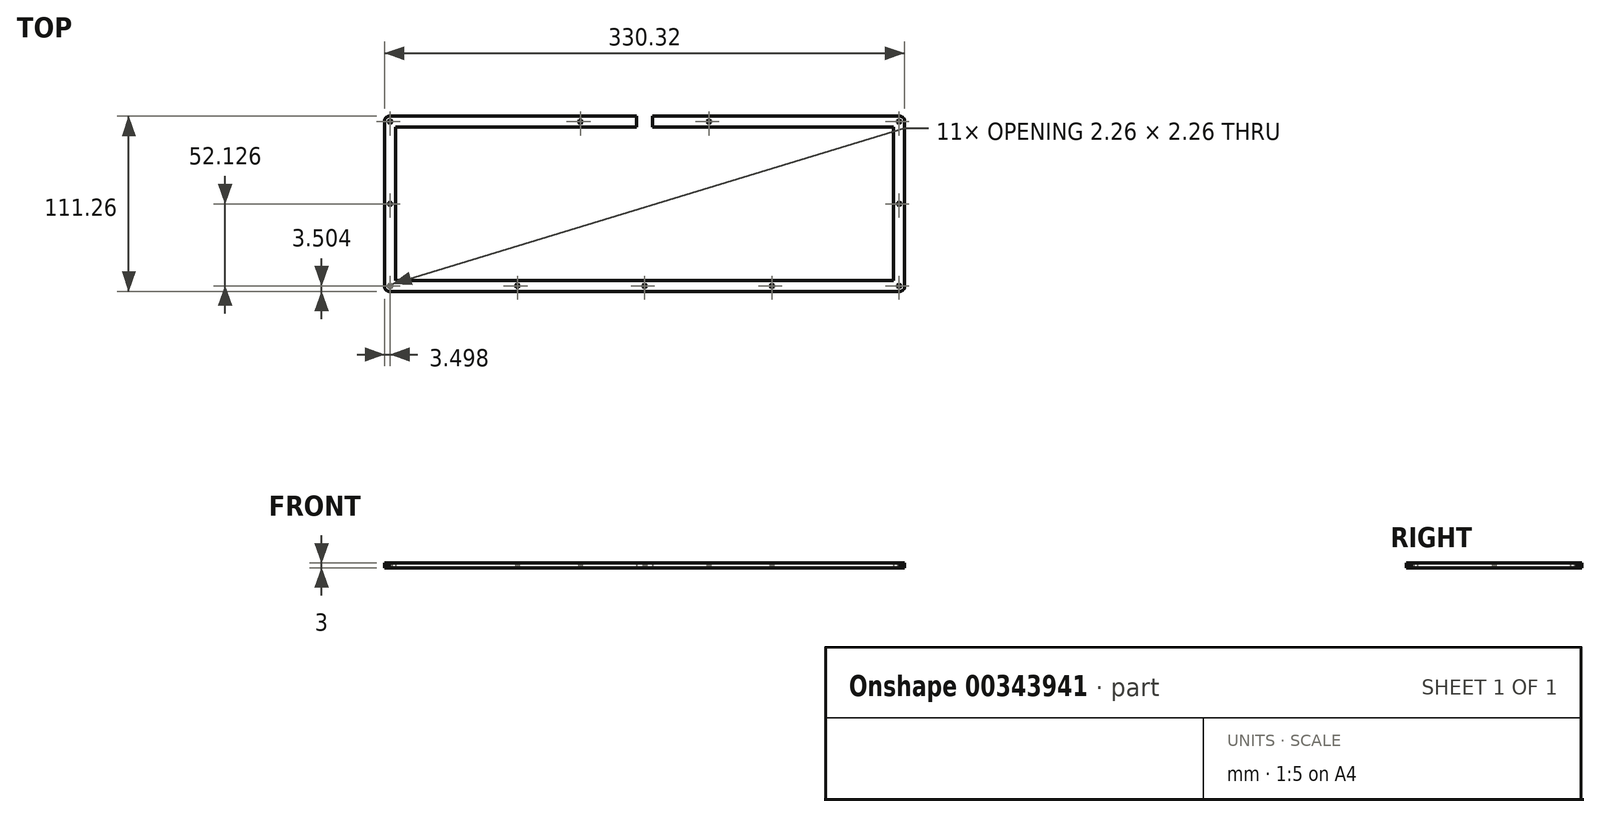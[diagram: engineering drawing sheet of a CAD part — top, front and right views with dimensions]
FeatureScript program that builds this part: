
annotation { "Feature Type Name" : "Feature", "Feature Type Description" : "" }
export const myFeature = defineFeature(function(context is Context, id is Id, definition is map)
    precondition{}
    {
        {
            var Q0;
            Q0=qCreatedBy(makeId("Top.planeOp"),FACE);
            var sketch = newSketch(context, id + "F0", { "sketchPlane" : qUnion([Q0])});
            skLineSegment(sketch, "E0", {"start": v(-5, 55.63) * mm, "end": v(-5, 48.62) * mm});
            skLineSegment(sketch, "E1", {"start": v(-5, 48.62) * mm, "end": v(-158.16, 48.62) * mm});
            skLineSegment(sketch, "E2", {"start": v(-158.16, 48.62) * mm, "end": v(-158.16, -48.63) * mm});
            skLineSegment(sketch, "E3", {"start": v(-158.16, -48.63) * mm, "end": v(158.16, -48.63) * mm});
            skLineSegment(sketch, "E4", {"start": v(158.16, -48.63) * mm, "end": v(158.16, 48.62) * mm});
            skLineSegment(sketch, "E5", {"start": v(158.16, 48.62) * mm, "end": v(5, 48.62) * mm});
            skLineSegment(sketch, "E6", {"start": v(5, 48.62) * mm, "end": v(5, 55.62) * mm});
            skLineSegment(sketch, "E7", {"start": v(5, 55.62) * mm, "end": v(162.16, 55.62) * mm});
            skLineSegment(sketch, "E8", {"start": v(162.16, 55.62) * mm, "end": v(162.4, 55.62) * mm});
            skLineSegment(sketch, "E9", {"start": v(162.4, 55.62) * mm, "end": v(162.63, 55.59) * mm});
            skLineSegment(sketch, "E10", {"start": v(162.63, 55.59) * mm, "end": v(162.86, 55.54) * mm});
            skLineSegment(sketch, "E11", {"start": v(162.86, 55.54) * mm, "end": v(163.1, 55.48) * mm});
            skLineSegment(sketch, "E12", {"start": v(163.1, 55.48) * mm, "end": v(163.31, 55.4) * mm});
            skLineSegment(sketch, "E13", {"start": v(163.31, 55.4) * mm, "end": v(163.53, 55.3) * mm});
            skLineSegment(sketch, "E14", {"start": v(163.53, 55.3) * mm, "end": v(163.73, 55.18) * mm});
            skLineSegment(sketch, "E15", {"start": v(163.73, 55.18) * mm, "end": v(163.93, 55.05) * mm});
            skLineSegment(sketch, "E16", {"start": v(163.93, 55.05) * mm, "end": v(164.11, 54.9) * mm});
            skLineSegment(sketch, "E17", {"start": v(164.11, 54.9) * mm, "end": v(164.29, 54.75) * mm});
            skLineSegment(sketch, "E18", {"start": v(164.29, 54.75) * mm, "end": v(164.45, 54.57) * mm});
            skLineSegment(sketch, "E19", {"start": v(164.45, 54.57) * mm, "end": v(164.6, 54.39) * mm});
            skLineSegment(sketch, "E20", {"start": v(164.6, 54.39) * mm, "end": v(164.72, 54.2) * mm});
            skLineSegment(sketch, "E21", {"start": v(164.72, 54.2) * mm, "end": v(164.84, 53.99) * mm});
            skLineSegment(sketch, "E22", {"start": v(164.84, 53.99) * mm, "end": v(164.93, 53.77) * mm});
            skLineSegment(sketch, "E23", {"start": v(164.93, 53.77) * mm, "end": v(165.02, 53.55) * mm});
            skLineSegment(sketch, "E24", {"start": v(165.02, 53.55) * mm, "end": v(165.08, 53.33) * mm});
            skLineSegment(sketch, "E25", {"start": v(165.08, 53.33) * mm, "end": v(165.13, 53.1) * mm});
            skLineSegment(sketch, "E26", {"start": v(165.13, 53.1) * mm, "end": v(165.15, 52.86) * mm});
            skLineSegment(sketch, "E27", {"start": v(165.15, 52.86) * mm, "end": v(165.16, 52.62) * mm});
            skLineSegment(sketch, "E28", {"start": v(165.16, 52.62) * mm, "end": v(165.16, -52.63) * mm});
            skLineSegment(sketch, "E29", {"start": v(165.16, -52.63) * mm, "end": v(165.15, -52.86) * mm});
            skLineSegment(sketch, "E30", {"start": v(165.15, -52.86) * mm, "end": v(165.13, -53.1) * mm});
            skLineSegment(sketch, "E31", {"start": v(165.13, -53.1) * mm, "end": v(165.08, -53.33) * mm});
            skLineSegment(sketch, "E32", {"start": v(165.08, -53.33) * mm, "end": v(165.02, -53.55) * mm});
            skLineSegment(sketch, "E33", {"start": v(165.02, -53.55) * mm, "end": v(164.93, -53.77) * mm});
            skLineSegment(sketch, "E34", {"start": v(164.93, -53.77) * mm, "end": v(164.84, -53.99) * mm});
            skLineSegment(sketch, "E35", {"start": v(164.84, -53.99) * mm, "end": v(164.72, -54.2) * mm});
            skLineSegment(sketch, "E36", {"start": v(164.72, -54.2) * mm, "end": v(164.6, -54.39) * mm});
            skLineSegment(sketch, "E37", {"start": v(164.6, -54.39) * mm, "end": v(164.45, -54.57) * mm});
            skLineSegment(sketch, "E38", {"start": v(164.45, -54.57) * mm, "end": v(164.29, -54.75) * mm});
            skLineSegment(sketch, "E39", {"start": v(164.29, -54.75) * mm, "end": v(164.11, -54.9) * mm});
            skLineSegment(sketch, "E40", {"start": v(164.11, -54.9) * mm, "end": v(163.93, -55.05) * mm});
            skLineSegment(sketch, "E41", {"start": v(163.93, -55.05) * mm, "end": v(163.73, -55.18) * mm});
            skLineSegment(sketch, "E42", {"start": v(163.73, -55.18) * mm, "end": v(163.53, -55.3) * mm});
            skLineSegment(sketch, "E43", {"start": v(163.53, -55.3) * mm, "end": v(163.31, -55.4) * mm});
            skLineSegment(sketch, "E44", {"start": v(163.31, -55.4) * mm, "end": v(163.1, -55.48) * mm});
            skLineSegment(sketch, "E45", {"start": v(163.1, -55.48) * mm, "end": v(162.86, -55.54) * mm});
            skLineSegment(sketch, "E46", {"start": v(162.86, -55.54) * mm, "end": v(162.63, -55.59) * mm});
            skLineSegment(sketch, "E47", {"start": v(162.63, -55.59) * mm, "end": v(162.4, -55.62) * mm});
            skLineSegment(sketch, "E48", {"start": v(162.4, -55.62) * mm, "end": v(162.16, -55.63) * mm});
            skLineSegment(sketch, "E49", {"start": v(162.16, -55.63) * mm, "end": v(-162.16, -55.63) * mm});
            skLineSegment(sketch, "E50", {"start": v(-162.16, -55.63) * mm, "end": v(-162.4, -55.62) * mm});
            skLineSegment(sketch, "E51", {"start": v(-162.4, -55.62) * mm, "end": v(-162.63, -55.59) * mm});
            skLineSegment(sketch, "E52", {"start": v(-162.63, -55.59) * mm, "end": v(-162.86, -55.54) * mm});
            skLineSegment(sketch, "E53", {"start": v(-162.86, -55.54) * mm, "end": v(-163.09, -55.48) * mm});
            skLineSegment(sketch, "E54", {"start": v(-163.09, -55.48) * mm, "end": v(-163.31, -55.4) * mm});
            skLineSegment(sketch, "E55", {"start": v(-163.31, -55.4) * mm, "end": v(-163.52, -55.3) * mm});
            skLineSegment(sketch, "E56", {"start": v(-163.52, -55.3) * mm, "end": v(-163.73, -55.18) * mm});
            skLineSegment(sketch, "E57", {"start": v(-163.73, -55.18) * mm, "end": v(-163.93, -55.05) * mm});
            skLineSegment(sketch, "E58", {"start": v(-163.93, -55.05) * mm, "end": v(-164.11, -54.9) * mm});
            skLineSegment(sketch, "E59", {"start": v(-164.11, -54.9) * mm, "end": v(-164.28, -54.75) * mm});
            skLineSegment(sketch, "E60", {"start": v(-164.28, -54.75) * mm, "end": v(-164.44, -54.57) * mm});
            skLineSegment(sketch, "E61", {"start": v(-164.44, -54.57) * mm, "end": v(-164.6, -54.39) * mm});
            skLineSegment(sketch, "E62", {"start": v(-164.6, -54.39) * mm, "end": v(-164.72, -54.2) * mm});
            skLineSegment(sketch, "E63", {"start": v(-164.72, -54.2) * mm, "end": v(-164.84, -53.99) * mm});
            skLineSegment(sketch, "E64", {"start": v(-164.84, -53.99) * mm, "end": v(-164.93, -53.77) * mm});
            skLineSegment(sketch, "E65", {"start": v(-164.93, -53.77) * mm, "end": v(-165.02, -53.55) * mm});
            skLineSegment(sketch, "E66", {"start": v(-165.02, -53.55) * mm, "end": v(-165.08, -53.33) * mm});
            skLineSegment(sketch, "E67", {"start": v(-165.08, -53.33) * mm, "end": v(-165.13, -53.1) * mm});
            skLineSegment(sketch, "E68", {"start": v(-165.13, -53.1) * mm, "end": v(-165.15, -52.86) * mm});
            skLineSegment(sketch, "E69", {"start": v(-165.15, -52.86) * mm, "end": v(-165.16, -52.63) * mm});
            skLineSegment(sketch, "E70", {"start": v(-165.16, -52.63) * mm, "end": v(-165.16, 52.62) * mm});
            skLineSegment(sketch, "E71", {"start": v(-165.16, 52.62) * mm, "end": v(-165.15, 52.86) * mm});
            skLineSegment(sketch, "E72", {"start": v(-165.15, 52.86) * mm, "end": v(-165.13, 53.1) * mm});
            skLineSegment(sketch, "E73", {"start": v(-165.13, 53.1) * mm, "end": v(-165.08, 53.33) * mm});
            skLineSegment(sketch, "E74", {"start": v(-165.08, 53.33) * mm, "end": v(-165.02, 53.55) * mm});
            skLineSegment(sketch, "E75", {"start": v(-165.02, 53.55) * mm, "end": v(-164.93, 53.77) * mm});
            skLineSegment(sketch, "E76", {"start": v(-164.93, 53.77) * mm, "end": v(-164.84, 53.99) * mm});
            skLineSegment(sketch, "E77", {"start": v(-164.84, 53.99) * mm, "end": v(-164.72, 54.2) * mm});
            skLineSegment(sketch, "E78", {"start": v(-164.72, 54.2) * mm, "end": v(-164.6, 54.39) * mm});
            skLineSegment(sketch, "E79", {"start": v(-164.6, 54.39) * mm, "end": v(-164.44, 54.57) * mm});
            skLineSegment(sketch, "E80", {"start": v(-164.44, 54.57) * mm, "end": v(-164.28, 54.75) * mm});
            skLineSegment(sketch, "E81", {"start": v(-164.28, 54.75) * mm, "end": v(-164.11, 54.9) * mm});
            skLineSegment(sketch, "E82", {"start": v(-164.11, 54.9) * mm, "end": v(-163.93, 55.05) * mm});
            skLineSegment(sketch, "E83", {"start": v(-163.93, 55.05) * mm, "end": v(-163.73, 55.18) * mm});
            skLineSegment(sketch, "E84", {"start": v(-163.73, 55.18) * mm, "end": v(-163.52, 55.3) * mm});
            skLineSegment(sketch, "E85", {"start": v(-163.52, 55.3) * mm, "end": v(-163.31, 55.4) * mm});
            skLineSegment(sketch, "E86", {"start": v(-163.31, 55.4) * mm, "end": v(-163.09, 55.48) * mm});
            skLineSegment(sketch, "E87", {"start": v(-163.09, 55.48) * mm, "end": v(-162.86, 55.54) * mm});
            skLineSegment(sketch, "E88", {"start": v(-162.86, 55.54) * mm, "end": v(-162.63, 55.59) * mm});
            skLineSegment(sketch, "E89", {"start": v(-162.63, 55.59) * mm, "end": v(-162.4, 55.62) * mm});
            skLineSegment(sketch, "E90", {"start": v(-162.4, 55.62) * mm, "end": v(-162.16, 55.63) * mm});
            skLineSegment(sketch, "E91", {"start": v(-162.16, 55.63) * mm, "end": v(-5, 55.63) * mm});
            skLineSegment(sketch, "E92", {"start": v(161.31, -51.05) * mm, "end": v(161, -51.21) * mm});
            skLineSegment(sketch, "E93", {"start": v(161, -51.21) * mm, "end": v(160.75, -51.46) * mm});
            skLineSegment(sketch, "E94", {"start": v(160.75, -51.46) * mm, "end": v(160.59, -51.78) * mm});
            skLineSegment(sketch, "E95", {"start": v(160.59, -51.78) * mm, "end": v(160.53, -52.13) * mm});
            skLineSegment(sketch, "E96", {"start": v(160.53, -52.13) * mm, "end": v(160.59, -52.48) * mm});
            skLineSegment(sketch, "E97", {"start": v(160.59, -52.48) * mm, "end": v(160.75, -52.79) * mm});
            skLineSegment(sketch, "E98", {"start": v(160.75, -52.79) * mm, "end": v(161, -53.04) * mm});
            skLineSegment(sketch, "E99", {"start": v(161, -53.04) * mm, "end": v(161.31, -53.2) * mm});
            skLineSegment(sketch, "E100", {"start": v(161.31, -53.2) * mm, "end": v(161.66, -53.26) * mm});
            skLineSegment(sketch, "E101", {"start": v(161.66, -53.26) * mm, "end": v(162.01, -53.2) * mm});
            skLineSegment(sketch, "E102", {"start": v(162.01, -53.2) * mm, "end": v(162.33, -53.04) * mm});
            skLineSegment(sketch, "E103", {"start": v(162.33, -53.04) * mm, "end": v(162.58, -52.79) * mm});
            skLineSegment(sketch, "E104", {"start": v(162.58, -52.79) * mm, "end": v(162.74, -52.48) * mm});
            skLineSegment(sketch, "E105", {"start": v(162.74, -52.48) * mm, "end": v(162.8, -52.13) * mm});
            skLineSegment(sketch, "E106", {"start": v(162.8, -52.13) * mm, "end": v(162.74, -51.78) * mm});
            skLineSegment(sketch, "E107", {"start": v(162.74, -51.78) * mm, "end": v(162.58, -51.46) * mm});
            skLineSegment(sketch, "E108", {"start": v(162.58, -51.46) * mm, "end": v(162.33, -51.21) * mm});
            skLineSegment(sketch, "E109", {"start": v(162.33, -51.21) * mm, "end": v(162.01, -51.05) * mm});
            skLineSegment(sketch, "E110", {"start": v(162.01, -51.05) * mm, "end": v(161.66, -51) * mm});
            skLineSegment(sketch, "E111", {"start": v(161.66, -51) * mm, "end": v(161.31, -51.05) * mm});
            skLineSegment(sketch, "E112", {"start": v(80.48, -51.05) * mm, "end": v(80.17, -51.21) * mm});
            skLineSegment(sketch, "E113", {"start": v(80.17, -51.21) * mm, "end": v(79.92, -51.46) * mm});
            skLineSegment(sketch, "E114", {"start": v(79.92, -51.46) * mm, "end": v(79.76, -51.78) * mm});
            skLineSegment(sketch, "E115", {"start": v(79.76, -51.78) * mm, "end": v(79.7, -52.13) * mm});
            skLineSegment(sketch, "E116", {"start": v(79.7, -52.13) * mm, "end": v(79.76, -52.48) * mm});
            skLineSegment(sketch, "E117", {"start": v(79.76, -52.48) * mm, "end": v(79.92, -52.79) * mm});
            skLineSegment(sketch, "E118", {"start": v(79.92, -52.79) * mm, "end": v(80.17, -53.04) * mm});
            skLineSegment(sketch, "E119", {"start": v(80.17, -53.04) * mm, "end": v(80.48, -53.2) * mm});
            skLineSegment(sketch, "E120", {"start": v(80.48, -53.2) * mm, "end": v(80.83, -53.26) * mm});
            skLineSegment(sketch, "E121", {"start": v(80.83, -53.26) * mm, "end": v(81.18, -53.2) * mm});
            skLineSegment(sketch, "E122", {"start": v(81.18, -53.2) * mm, "end": v(81.5, -53.04) * mm});
            skLineSegment(sketch, "E123", {"start": v(81.5, -53.04) * mm, "end": v(81.75, -52.79) * mm});
            skLineSegment(sketch, "E124", {"start": v(81.75, -52.79) * mm, "end": v(81.9, -52.48) * mm});
            skLineSegment(sketch, "E125", {"start": v(81.9, -52.48) * mm, "end": v(81.96, -52.13) * mm});
            skLineSegment(sketch, "E126", {"start": v(81.96, -52.13) * mm, "end": v(81.9, -51.78) * mm});
            skLineSegment(sketch, "E127", {"start": v(81.9, -51.78) * mm, "end": v(81.75, -51.46) * mm});
            skLineSegment(sketch, "E128", {"start": v(81.75, -51.46) * mm, "end": v(81.5, -51.21) * mm});
            skLineSegment(sketch, "E129", {"start": v(81.5, -51.21) * mm, "end": v(81.18, -51.05) * mm});
            skLineSegment(sketch, "E130", {"start": v(81.18, -51.05) * mm, "end": v(80.83, -51) * mm});
            skLineSegment(sketch, "E131", {"start": v(80.83, -51) * mm, "end": v(80.48, -51.05) * mm});
            skLineSegment(sketch, "E132", {"start": v(-0.35, -51.05) * mm, "end": v(-0.66, -51.21) * mm});
            skLineSegment(sketch, "E133", {"start": v(-0.66, -51.21) * mm, "end": v(-0.91, -51.46) * mm});
            skLineSegment(sketch, "E134", {"start": v(-0.91, -51.46) * mm, "end": v(-1.07, -51.78) * mm});
            skLineSegment(sketch, "E135", {"start": v(-1.07, -51.78) * mm, "end": v(-1.13, -52.13) * mm});
            skLineSegment(sketch, "E136", {"start": v(-1.13, -52.13) * mm, "end": v(-1.07, -52.48) * mm});
            skLineSegment(sketch, "E137", {"start": v(-1.07, -52.48) * mm, "end": v(-0.91, -52.79) * mm});
            skLineSegment(sketch, "E138", {"start": v(-0.91, -52.79) * mm, "end": v(-0.66, -53.04) * mm});
            skLineSegment(sketch, "E139", {"start": v(-0.66, -53.04) * mm, "end": v(-0.35, -53.2) * mm});
            skLineSegment(sketch, "E140", {"start": v(-0.35, -53.2) * mm, "end": v(0, -53.26) * mm});
            skLineSegment(sketch, "E141", {"start": v(0, -53.26) * mm, "end": v(0.35, -53.2) * mm});
            skLineSegment(sketch, "E142", {"start": v(0.35, -53.2) * mm, "end": v(0.67, -53.04) * mm});
            skLineSegment(sketch, "E143", {"start": v(0.67, -53.04) * mm, "end": v(0.92, -52.79) * mm});
            skLineSegment(sketch, "E144", {"start": v(0.92, -52.79) * mm, "end": v(1.07, -52.48) * mm});
            skLineSegment(sketch, "E145", {"start": v(1.07, -52.48) * mm, "end": v(1.13, -52.13) * mm});
            skLineSegment(sketch, "E146", {"start": v(1.13, -52.13) * mm, "end": v(1.07, -51.78) * mm});
            skLineSegment(sketch, "E147", {"start": v(1.07, -51.78) * mm, "end": v(0.92, -51.46) * mm});
            skLineSegment(sketch, "E148", {"start": v(0.92, -51.46) * mm, "end": v(0.67, -51.21) * mm});
            skLineSegment(sketch, "E149", {"start": v(0.67, -51.21) * mm, "end": v(0.35, -51.05) * mm});
            skLineSegment(sketch, "E150", {"start": v(0.35, -51.05) * mm, "end": v(0, -51) * mm});
            skLineSegment(sketch, "E151", {"start": v(0, -51) * mm, "end": v(-0.35, -51.05) * mm});
            skLineSegment(sketch, "E152", {"start": v(-81.18, -51.05) * mm, "end": v(-81.5, -51.21) * mm});
            skLineSegment(sketch, "E153", {"start": v(-81.5, -51.21) * mm, "end": v(-81.75, -51.46) * mm});
            skLineSegment(sketch, "E154", {"start": v(-81.75, -51.46) * mm, "end": v(-81.9, -51.78) * mm});
            skLineSegment(sketch, "E155", {"start": v(-81.9, -51.78) * mm, "end": v(-81.96, -52.13) * mm});
            skLineSegment(sketch, "E156", {"start": v(-81.96, -52.13) * mm, "end": v(-81.9, -52.48) * mm});
            skLineSegment(sketch, "E157", {"start": v(-81.9, -52.48) * mm, "end": v(-81.75, -52.79) * mm});
            skLineSegment(sketch, "E158", {"start": v(-81.75, -52.79) * mm, "end": v(-81.5, -53.04) * mm});
            skLineSegment(sketch, "E159", {"start": v(-81.5, -53.04) * mm, "end": v(-81.18, -53.2) * mm});
            skLineSegment(sketch, "E160", {"start": v(-81.18, -53.2) * mm, "end": v(-80.83, -53.26) * mm});
            skLineSegment(sketch, "E161", {"start": v(-80.83, -53.26) * mm, "end": v(-80.48, -53.2) * mm});
            skLineSegment(sketch, "E162", {"start": v(-80.48, -53.2) * mm, "end": v(-80.17, -53.04) * mm});
            skLineSegment(sketch, "E163", {"start": v(-80.17, -53.04) * mm, "end": v(-79.92, -52.79) * mm});
            skLineSegment(sketch, "E164", {"start": v(-79.92, -52.79) * mm, "end": v(-79.76, -52.48) * mm});
            skLineSegment(sketch, "E165", {"start": v(-79.76, -52.48) * mm, "end": v(-79.7, -52.13) * mm});
            skLineSegment(sketch, "E166", {"start": v(-79.7, -52.13) * mm, "end": v(-79.76, -51.78) * mm});
            skLineSegment(sketch, "E167", {"start": v(-79.76, -51.78) * mm, "end": v(-79.92, -51.46) * mm});
            skLineSegment(sketch, "E168", {"start": v(-79.92, -51.46) * mm, "end": v(-80.17, -51.21) * mm});
            skLineSegment(sketch, "E169", {"start": v(-80.17, -51.21) * mm, "end": v(-80.48, -51.05) * mm});
            skLineSegment(sketch, "E170", {"start": v(-80.48, -51.05) * mm, "end": v(-80.83, -51) * mm});
            skLineSegment(sketch, "E171", {"start": v(-80.83, -51) * mm, "end": v(-81.18, -51.05) * mm});
            skLineSegment(sketch, "E172", {"start": v(-162.01, -51.05) * mm, "end": v(-162.33, -51.21) * mm});
            skLineSegment(sketch, "E173", {"start": v(-162.33, -51.21) * mm, "end": v(-162.58, -51.46) * mm});
            skLineSegment(sketch, "E174", {"start": v(-162.58, -51.46) * mm, "end": v(-162.74, -51.78) * mm});
            skLineSegment(sketch, "E175", {"start": v(-162.74, -51.78) * mm, "end": v(-162.8, -52.13) * mm});
            skLineSegment(sketch, "E176", {"start": v(-162.8, -52.13) * mm, "end": v(-162.74, -52.48) * mm});
            skLineSegment(sketch, "E177", {"start": v(-162.74, -52.48) * mm, "end": v(-162.58, -52.79) * mm});
            skLineSegment(sketch, "E178", {"start": v(-162.58, -52.79) * mm, "end": v(-162.33, -53.04) * mm});
            skLineSegment(sketch, "E179", {"start": v(-162.33, -53.04) * mm, "end": v(-162.01, -53.2) * mm});
            skLineSegment(sketch, "E180", {"start": v(-162.01, -53.2) * mm, "end": v(-161.66, -53.26) * mm});
            skLineSegment(sketch, "E181", {"start": v(-161.66, -53.26) * mm, "end": v(-161.31, -53.2) * mm});
            skLineSegment(sketch, "E182", {"start": v(-161.31, -53.2) * mm, "end": v(-161, -53.04) * mm});
            skLineSegment(sketch, "E183", {"start": v(-161, -53.04) * mm, "end": v(-160.75, -52.79) * mm});
            skLineSegment(sketch, "E184", {"start": v(-160.75, -52.79) * mm, "end": v(-160.59, -52.48) * mm});
            skLineSegment(sketch, "E185", {"start": v(-160.59, -52.48) * mm, "end": v(-160.53, -52.13) * mm});
            skLineSegment(sketch, "E186", {"start": v(-160.53, -52.13) * mm, "end": v(-160.59, -51.78) * mm});
            skLineSegment(sketch, "E187", {"start": v(-160.59, -51.78) * mm, "end": v(-160.75, -51.46) * mm});
            skLineSegment(sketch, "E188", {"start": v(-160.75, -51.46) * mm, "end": v(-161, -51.21) * mm});
            skLineSegment(sketch, "E189", {"start": v(-161, -51.21) * mm, "end": v(-161.31, -51.05) * mm});
            skLineSegment(sketch, "E190", {"start": v(-161.31, -51.05) * mm, "end": v(-161.66, -51) * mm});
            skLineSegment(sketch, "E191", {"start": v(-161.66, -51) * mm, "end": v(-162.01, -51.05) * mm});
            skLineSegment(sketch, "E192", {"start": v(161.31, 1.08) * mm, "end": v(161, 0.91) * mm});
            skLineSegment(sketch, "E193", {"start": v(161, 0.91) * mm, "end": v(160.75, 0.66) * mm});
            skLineSegment(sketch, "E194", {"start": v(160.75, 0.66) * mm, "end": v(160.59, 0.35) * mm});
            skLineSegment(sketch, "E195", {"start": v(160.59, 0.35) * mm, "end": v(160.53, 0) * mm});
            skLineSegment(sketch, "E196", {"start": v(160.53, 0) * mm, "end": v(160.59, -0.35) * mm});
            skLineSegment(sketch, "E197", {"start": v(160.59, -0.35) * mm, "end": v(160.75, -0.66) * mm});
            skLineSegment(sketch, "E198", {"start": v(160.75, -0.66) * mm, "end": v(161, -0.91) * mm});
            skLineSegment(sketch, "E199", {"start": v(161, -0.91) * mm, "end": v(161.31, -1.07) * mm});
            skLineSegment(sketch, "E200", {"start": v(161.31, -1.07) * mm, "end": v(161.66, -1.13) * mm});
            skLineSegment(sketch, "E201", {"start": v(161.66, -1.13) * mm, "end": v(162.01, -1.07) * mm});
            skLineSegment(sketch, "E202", {"start": v(162.01, -1.07) * mm, "end": v(162.33, -0.91) * mm});
            skLineSegment(sketch, "E203", {"start": v(162.33, -0.91) * mm, "end": v(162.58, -0.66) * mm});
            skLineSegment(sketch, "E204", {"start": v(162.58, -0.66) * mm, "end": v(162.74, -0.35) * mm});
            skLineSegment(sketch, "E205", {"start": v(162.74, -0.35) * mm, "end": v(162.8, 0) * mm});
            skLineSegment(sketch, "E206", {"start": v(162.8, 0) * mm, "end": v(162.74, 0.35) * mm});
            skLineSegment(sketch, "E207", {"start": v(162.74, 0.35) * mm, "end": v(162.58, 0.66) * mm});
            skLineSegment(sketch, "E208", {"start": v(162.58, 0.66) * mm, "end": v(162.33, 0.91) * mm});
            skLineSegment(sketch, "E209", {"start": v(162.33, 0.91) * mm, "end": v(162.01, 1.08) * mm});
            skLineSegment(sketch, "E210", {"start": v(162.01, 1.08) * mm, "end": v(161.66, 1.13) * mm});
            skLineSegment(sketch, "E211", {"start": v(161.66, 1.13) * mm, "end": v(161.31, 1.08) * mm});
            skLineSegment(sketch, "E212", {"start": v(-162.01, 1.08) * mm, "end": v(-162.33, 0.91) * mm});
            skLineSegment(sketch, "E213", {"start": v(-162.33, 0.91) * mm, "end": v(-162.58, 0.66) * mm});
            skLineSegment(sketch, "E214", {"start": v(-162.58, 0.66) * mm, "end": v(-162.74, 0.35) * mm});
            skLineSegment(sketch, "E215", {"start": v(-162.74, 0.35) * mm, "end": v(-162.8, 0) * mm});
            skLineSegment(sketch, "E216", {"start": v(-162.8, 0) * mm, "end": v(-162.74, -0.35) * mm});
            skLineSegment(sketch, "E217", {"start": v(-162.74, -0.35) * mm, "end": v(-162.58, -0.66) * mm});
            skLineSegment(sketch, "E218", {"start": v(-162.58, -0.66) * mm, "end": v(-162.33, -0.91) * mm});
            skLineSegment(sketch, "E219", {"start": v(-162.33, -0.91) * mm, "end": v(-162.01, -1.07) * mm});
            skLineSegment(sketch, "E220", {"start": v(-162.01, -1.07) * mm, "end": v(-161.66, -1.13) * mm});
            skLineSegment(sketch, "E221", {"start": v(-161.66, -1.13) * mm, "end": v(-161.31, -1.07) * mm});
            skLineSegment(sketch, "E222", {"start": v(-161.31, -1.07) * mm, "end": v(-161, -0.91) * mm});
            skLineSegment(sketch, "E223", {"start": v(-161, -0.91) * mm, "end": v(-160.75, -0.66) * mm});
            skLineSegment(sketch, "E224", {"start": v(-160.75, -0.66) * mm, "end": v(-160.59, -0.35) * mm});
            skLineSegment(sketch, "E225", {"start": v(-160.59, -0.35) * mm, "end": v(-160.53, 0) * mm});
            skLineSegment(sketch, "E226", {"start": v(-160.53, 0) * mm, "end": v(-160.59, 0.35) * mm});
            skLineSegment(sketch, "E227", {"start": v(-160.59, 0.35) * mm, "end": v(-160.75, 0.66) * mm});
            skLineSegment(sketch, "E228", {"start": v(-160.75, 0.66) * mm, "end": v(-161, 0.91) * mm});
            skLineSegment(sketch, "E229", {"start": v(-161, 0.91) * mm, "end": v(-161.31, 1.08) * mm});
            skLineSegment(sketch, "E230", {"start": v(-161.31, 1.08) * mm, "end": v(-161.66, 1.13) * mm});
            skLineSegment(sketch, "E231", {"start": v(-161.66, 1.13) * mm, "end": v(-162.01, 1.08) * mm});
            skLineSegment(sketch, "E232", {"start": v(-41.18, 53.2) * mm, "end": v(-41.5, 53.04) * mm});
            skLineSegment(sketch, "E233", {"start": v(-41.5, 53.04) * mm, "end": v(-41.75, 52.8) * mm});
            skLineSegment(sketch, "E234", {"start": v(-41.75, 52.8) * mm, "end": v(-41.9, 52.47) * mm});
            skLineSegment(sketch, "E235", {"start": v(-41.9, 52.47) * mm, "end": v(-41.96, 52.12) * mm});
            skLineSegment(sketch, "E236", {"start": v(-41.96, 52.12) * mm, "end": v(-41.9, 51.78) * mm});
            skLineSegment(sketch, "E237", {"start": v(-41.9, 51.78) * mm, "end": v(-41.75, 51.46) * mm});
            skLineSegment(sketch, "E238", {"start": v(-41.75, 51.46) * mm, "end": v(-41.5, 51.21) * mm});
            skLineSegment(sketch, "E239", {"start": v(-41.5, 51.21) * mm, "end": v(-41.18, 51.05) * mm});
            skLineSegment(sketch, "E240", {"start": v(-41.18, 51.05) * mm, "end": v(-40.83, 51) * mm});
            skLineSegment(sketch, "E241", {"start": v(-40.83, 51) * mm, "end": v(-40.48, 51.05) * mm});
            skLineSegment(sketch, "E242", {"start": v(-40.48, 51.05) * mm, "end": v(-40.17, 51.21) * mm});
            skLineSegment(sketch, "E243", {"start": v(-40.17, 51.21) * mm, "end": v(-39.92, 51.46) * mm});
            skLineSegment(sketch, "E244", {"start": v(-39.92, 51.46) * mm, "end": v(-39.76, 51.78) * mm});
            skLineSegment(sketch, "E245", {"start": v(-39.76, 51.78) * mm, "end": v(-39.7, 52.12) * mm});
            skLineSegment(sketch, "E246", {"start": v(-39.7, 52.12) * mm, "end": v(-39.76, 52.47) * mm});
            skLineSegment(sketch, "E247", {"start": v(-39.76, 52.47) * mm, "end": v(-39.92, 52.8) * mm});
            skLineSegment(sketch, "E248", {"start": v(-39.92, 52.8) * mm, "end": v(-40.17, 53.04) * mm});
            skLineSegment(sketch, "E249", {"start": v(-40.17, 53.04) * mm, "end": v(-40.48, 53.2) * mm});
            skLineSegment(sketch, "E250", {"start": v(-40.48, 53.2) * mm, "end": v(-40.83, 53.26) * mm});
            skLineSegment(sketch, "E251", {"start": v(-40.83, 53.26) * mm, "end": v(-41.18, 53.2) * mm});
            skLineSegment(sketch, "E252", {"start": v(40.48, 53.2) * mm, "end": v(40.17, 53.04) * mm});
            skLineSegment(sketch, "E253", {"start": v(40.17, 53.04) * mm, "end": v(39.92, 52.8) * mm});
            skLineSegment(sketch, "E254", {"start": v(39.92, 52.8) * mm, "end": v(39.76, 52.47) * mm});
            skLineSegment(sketch, "E255", {"start": v(39.76, 52.47) * mm, "end": v(39.7, 52.12) * mm});
            skLineSegment(sketch, "E256", {"start": v(39.7, 52.12) * mm, "end": v(39.76, 51.78) * mm});
            skLineSegment(sketch, "E257", {"start": v(39.76, 51.78) * mm, "end": v(39.92, 51.46) * mm});
            skLineSegment(sketch, "E258", {"start": v(39.92, 51.46) * mm, "end": v(40.17, 51.21) * mm});
            skLineSegment(sketch, "E259", {"start": v(40.17, 51.21) * mm, "end": v(40.48, 51.05) * mm});
            skLineSegment(sketch, "E260", {"start": v(40.48, 51.05) * mm, "end": v(40.83, 51) * mm});
            skLineSegment(sketch, "E261", {"start": v(40.83, 51) * mm, "end": v(41.18, 51.05) * mm});
            skLineSegment(sketch, "E262", {"start": v(41.18, 51.05) * mm, "end": v(41.5, 51.21) * mm});
            skLineSegment(sketch, "E263", {"start": v(41.5, 51.21) * mm, "end": v(41.75, 51.46) * mm});
            skLineSegment(sketch, "E264", {"start": v(41.75, 51.46) * mm, "end": v(41.9, 51.78) * mm});
            skLineSegment(sketch, "E265", {"start": v(41.9, 51.78) * mm, "end": v(41.96, 52.12) * mm});
            skLineSegment(sketch, "E266", {"start": v(41.96, 52.12) * mm, "end": v(41.9, 52.47) * mm});
            skLineSegment(sketch, "E267", {"start": v(41.9, 52.47) * mm, "end": v(41.75, 52.8) * mm});
            skLineSegment(sketch, "E268", {"start": v(41.75, 52.8) * mm, "end": v(41.5, 53.04) * mm});
            skLineSegment(sketch, "E269", {"start": v(41.5, 53.04) * mm, "end": v(41.18, 53.2) * mm});
            skLineSegment(sketch, "E270", {"start": v(41.18, 53.2) * mm, "end": v(40.83, 53.26) * mm});
            skLineSegment(sketch, "E271", {"start": v(40.83, 53.26) * mm, "end": v(40.48, 53.2) * mm});
            skLineSegment(sketch, "E272", {"start": v(161.31, 53.2) * mm, "end": v(161, 53.04) * mm});
            skLineSegment(sketch, "E273", {"start": v(161, 53.04) * mm, "end": v(160.75, 52.8) * mm});
            skLineSegment(sketch, "E274", {"start": v(160.75, 52.8) * mm, "end": v(160.59, 52.47) * mm});
            skLineSegment(sketch, "E275", {"start": v(160.59, 52.47) * mm, "end": v(160.53, 52.12) * mm});
            skLineSegment(sketch, "E276", {"start": v(160.53, 52.12) * mm, "end": v(160.59, 51.78) * mm});
            skLineSegment(sketch, "E277", {"start": v(160.59, 51.78) * mm, "end": v(160.75, 51.46) * mm});
            skLineSegment(sketch, "E278", {"start": v(160.75, 51.46) * mm, "end": v(161, 51.21) * mm});
            skLineSegment(sketch, "E279", {"start": v(161, 51.21) * mm, "end": v(161.31, 51.05) * mm});
            skLineSegment(sketch, "E280", {"start": v(161.31, 51.05) * mm, "end": v(161.66, 51) * mm});
            skLineSegment(sketch, "E281", {"start": v(161.66, 51) * mm, "end": v(162.01, 51.05) * mm});
            skLineSegment(sketch, "E282", {"start": v(162.01, 51.05) * mm, "end": v(162.33, 51.21) * mm});
            skLineSegment(sketch, "E283", {"start": v(162.33, 51.21) * mm, "end": v(162.58, 51.46) * mm});
            skLineSegment(sketch, "E284", {"start": v(162.58, 51.46) * mm, "end": v(162.74, 51.78) * mm});
            skLineSegment(sketch, "E285", {"start": v(162.74, 51.78) * mm, "end": v(162.8, 52.12) * mm});
            skLineSegment(sketch, "E286", {"start": v(162.8, 52.12) * mm, "end": v(162.74, 52.47) * mm});
            skLineSegment(sketch, "E287", {"start": v(162.74, 52.47) * mm, "end": v(162.58, 52.8) * mm});
            skLineSegment(sketch, "E288", {"start": v(162.58, 52.8) * mm, "end": v(162.33, 53.04) * mm});
            skLineSegment(sketch, "E289", {"start": v(162.33, 53.04) * mm, "end": v(162.01, 53.2) * mm});
            skLineSegment(sketch, "E290", {"start": v(162.01, 53.2) * mm, "end": v(161.66, 53.26) * mm});
            skLineSegment(sketch, "E291", {"start": v(161.66, 53.26) * mm, "end": v(161.31, 53.2) * mm});
            skLineSegment(sketch, "E292", {"start": v(-162.01, 53.2) * mm, "end": v(-162.33, 53.04) * mm});
            skLineSegment(sketch, "E293", {"start": v(-162.33, 53.04) * mm, "end": v(-162.58, 52.8) * mm});
            skLineSegment(sketch, "E294", {"start": v(-162.58, 52.8) * mm, "end": v(-162.74, 52.47) * mm});
            skLineSegment(sketch, "E295", {"start": v(-162.74, 52.47) * mm, "end": v(-162.8, 52.12) * mm});
            skLineSegment(sketch, "E296", {"start": v(-162.8, 52.12) * mm, "end": v(-162.74, 51.78) * mm});
            skLineSegment(sketch, "E297", {"start": v(-162.74, 51.78) * mm, "end": v(-162.58, 51.46) * mm});
            skLineSegment(sketch, "E298", {"start": v(-162.58, 51.46) * mm, "end": v(-162.33, 51.21) * mm});
            skLineSegment(sketch, "E299", {"start": v(-162.33, 51.21) * mm, "end": v(-162.01, 51.05) * mm});
            skLineSegment(sketch, "E300", {"start": v(-162.01, 51.05) * mm, "end": v(-161.66, 51) * mm});
            skLineSegment(sketch, "E301", {"start": v(-161.66, 51) * mm, "end": v(-161.31, 51.05) * mm});
            skLineSegment(sketch, "E302", {"start": v(-161.31, 51.05) * mm, "end": v(-161, 51.21) * mm});
            skLineSegment(sketch, "E303", {"start": v(-161, 51.21) * mm, "end": v(-160.75, 51.46) * mm});
            skLineSegment(sketch, "E304", {"start": v(-160.75, 51.46) * mm, "end": v(-160.59, 51.78) * mm});
            skLineSegment(sketch, "E305", {"start": v(-160.59, 51.78) * mm, "end": v(-160.53, 52.12) * mm});
            skLineSegment(sketch, "E306", {"start": v(-160.53, 52.12) * mm, "end": v(-160.59, 52.47) * mm});
            skLineSegment(sketch, "E307", {"start": v(-160.59, 52.47) * mm, "end": v(-160.75, 52.8) * mm});
            skLineSegment(sketch, "E308", {"start": v(-160.75, 52.8) * mm, "end": v(-161, 53.04) * mm});
            skLineSegment(sketch, "E309", {"start": v(-161, 53.04) * mm, "end": v(-161.31, 53.2) * mm});
            skLineSegment(sketch, "E310", {"start": v(-161.31, 53.2) * mm, "end": v(-161.66, 53.26) * mm});
            skLineSegment(sketch, "E311", {"start": v(-161.66, 53.26) * mm, "end": v(-162.01, 53.2) * mm});
            skSolve(sketch);
        }
        {
            var Q0;
            Q0 = qSketchRegion(id + "F0", true);
            extrude(context, id + "F1", {"entities" : qUnion([Q0]), "depth" : 3 * mm});
        }
    });
